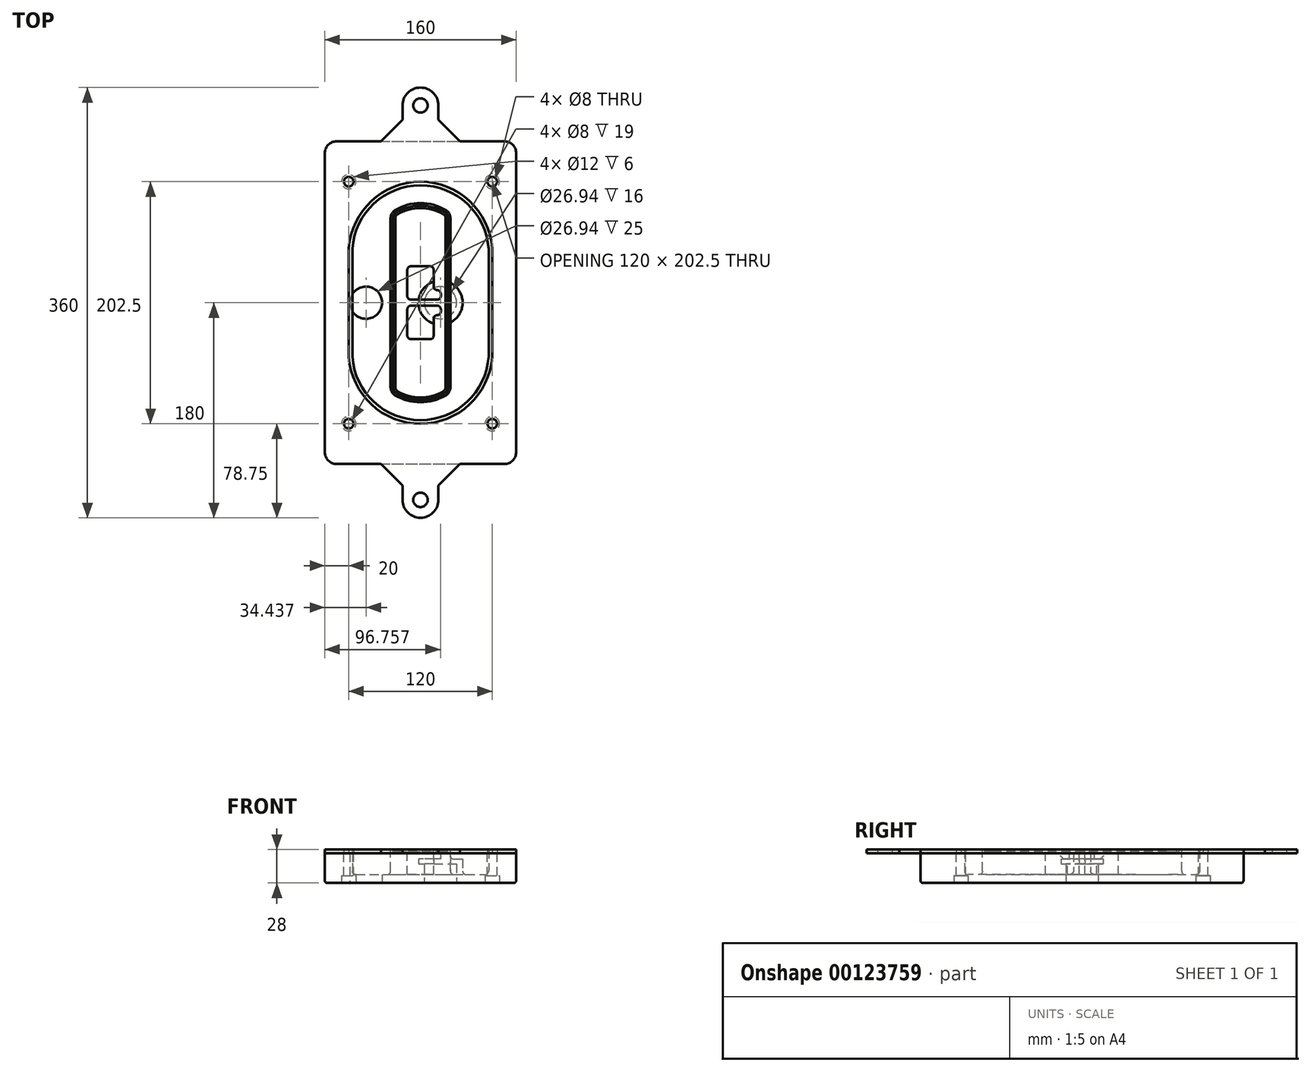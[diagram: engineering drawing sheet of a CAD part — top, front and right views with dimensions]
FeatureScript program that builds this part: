
annotation { "Feature Type Name" : "Feature", "Feature Type Description" : "" }
export const myFeature = defineFeature(function(context is Context, id is Id, definition is map)
    precondition{}
    {
        {
            var Q0;
            Q0=qCreatedBy(makeId("Top.planeOp"),FACE);
            var sketch = newSketch(context, id + "F0", { "sketchPlane" : qUnion([Q0])});
            skPoint(sketch, "E0.rect.middle", {"position": v(0, 0) * mm});
            skLineSegment(sketch, "E1.bottom", {"start": v(-70, -135) * mm, "end": v(70, -135) * mm});
            skLineSegment(sketch, "E1.top", {"start": v(-70, 135) * mm, "end": v(70, 135) * mm});
            skLineSegment(sketch, "E1.left", {"start": v(-80, -125) * mm, "end": v(-80, 125) * mm});
            skLineSegment(sketch, "E1.right", {"start": v(80, -125) * mm, "end": v(80, 125) * mm});
            skLineSegment(sketch, "E2", {"start": v(-80, 135) * mm, "end": v(80, -135) * mm, "construction": true});
            skLineSegment(sketch, "E3", {"start": v(80, 135) * mm, "end": v(-80, -135) * mm, "construction": true});
            skCircle(sketch, "E4", {"center": v(-60, 101.25) * mm, "radius": 4 * mm});
            skCircle(sketch, "E5", {"center": v(60, 101.25) * mm, "radius": 4 * mm});
            skCircle(sketch, "E6", {"center": v(60, -101.25) * mm, "radius": 4 * mm});
            skCircle(sketch, "E7", {"center": v(-60, -101.25) * mm, "radius": 4 * mm});
            skLineSegment(sketch, "E8", {"start": v(-60, 101.25) * mm, "end": v(60, 101.25) * mm, "construction": true});
            skLineSegment(sketch, "E9", {"start": v(60, 101.25) * mm, "end": v(60, -101.25) * mm, "construction": true});
            skLineSegment(sketch, "E10", {"start": v(60, -101.25) * mm, "end": v(-60, -101.25) * mm, "construction": true});
            skLineSegment(sketch, "E11", {"start": v(-60, -101.25) * mm, "end": v(-60, 101.25) * mm, "construction": true});
            skLineSegment(sketch, "E12", {"start": v(-60, 44.66) * mm, "end": v(-60, -44.66) * mm});
            skLineSegment(sketch, "E13", {"start": v(60, 44.66) * mm, "end": v(60, -44.66) * mm});
            skArc(sketch, "E14", {"start": v(59.98, 45.37) * mm, "mid": v(0, 101.25) * mm, "end": v(-59.98, 45.37) * mm});
            skArc(sketch, "E15", {"start": v(-59.98, -45.37) * mm, "mid": v(0, -101.25) * mm, "end": v(59.98, -45.37) * mm});
            skLineSegment(sketch, "E16", {"start": v(-60, 0) * mm, "end": v(60, 0) * mm, "construction": true});
            skPoint(sketch, "E17.visualSharp", {"position": v(-60, -45) * mm});
            skArc(sketch, "E17.filletArc", {"start": v(-60, -44.66) * mm, "mid": v(-60, -45.02) * mm, "end": v(-59.98, -45.37) * mm});
            skPoint(sketch, "E18.visualSharp", {"position": v(-60, 45) * mm});
            skArc(sketch, "E18.filletArc", {"start": v(-59.98, 45.37) * mm, "mid": v(-60, 45.02) * mm, "end": v(-60, 44.66) * mm});
            skPoint(sketch, "E19.visualSharp", {"position": v(60, 45) * mm});
            skArc(sketch, "E19.filletArc", {"start": v(60, 44.66) * mm, "mid": v(60, 45.02) * mm, "end": v(59.98, 45.37) * mm});
            skPoint(sketch, "E20.visualSharp", {"position": v(60, -45) * mm});
            skArc(sketch, "E20.filletArc", {"start": v(59.98, -45.37) * mm, "mid": v(60, -45.02) * mm, "end": v(60, -44.66) * mm});
            skPoint(sketch, "E21.visualSharp", {"position": v(-80, 135) * mm});
            skArc(sketch, "E21.filletArc", {"start": v(-70, 135) * mm, "mid": v(-77.07, 132.07) * mm, "end": v(-80, 125) * mm});
            skPoint(sketch, "E22.visualSharp", {"position": v(80, 135) * mm});
            skArc(sketch, "E22.filletArc", {"start": v(80, 125) * mm, "mid": v(77.07, 132.07) * mm, "end": v(70, 135) * mm});
            skPoint(sketch, "E23.visualSharp", {"position": v(80, -135) * mm});
            skArc(sketch, "E23.filletArc", {"start": v(70, -135) * mm, "mid": v(77.07, -132.07) * mm, "end": v(80, -125) * mm});
            skPoint(sketch, "E24.visualSharp", {"position": v(-80, -135) * mm});
            skArc(sketch, "E24.filletArc", {"start": v(-80, -125) * mm, "mid": v(-77.07, -132.07) * mm, "end": v(-70, -135) * mm});
            skArc(sketch, "E25.0", {"start": v(57, 44.66) * mm, "mid": v(57, 44.9) * mm, "end": v(56.98, 45.16) * mm});
            skLineSegment(sketch, "E25.1", {"start": v(57, 44.66) * mm, "end": v(57, -44.66) * mm});
            skArc(sketch, "E25.2", {"start": v(56.98, -45.16) * mm, "mid": v(57, -44.9) * mm, "end": v(57, -44.66) * mm});
            skArc(sketch, "E25.3", {"start": v(-56.98, -45.16) * mm, "mid": v(0, -98.25) * mm, "end": v(56.98, -45.16) * mm});
            skArc(sketch, "E25.4", {"start": v(-57, -44.66) * mm, "mid": v(-57, -44.9) * mm, "end": v(-56.98, -45.16) * mm});
            skArc(sketch, "E25.5", {"start": v(56.98, 45.16) * mm, "mid": v(0, 98.25) * mm, "end": v(-56.98, 45.16) * mm});
            skLineSegment(sketch, "E25.6", {"start": v(-57, 44.66) * mm, "end": v(-57, -44.66) * mm});
            skArc(sketch, "E25.7", {"start": v(-56.98, 45.16) * mm, "mid": v(-57, 44.9) * mm, "end": v(-57, 44.66) * mm});
            skArc(sketch, "E26.0", {"start": v(-63.97, 45.65) * mm, "mid": v(-64, 45.16) * mm, "end": v(-64, 44.66) * mm});
            skArc(sketch, "E26.1", {"start": v(63.97, 45.65) * mm, "mid": v(0, 105.25) * mm, "end": v(-63.97, 45.65) * mm});
            skArc(sketch, "E26.2", {"start": v(64, 44.66) * mm, "mid": v(64, 45.16) * mm, "end": v(63.97, 45.65) * mm});
            skLineSegment(sketch, "E26.3", {"start": v(64, 44.66) * mm, "end": v(64, -44.66) * mm});
            skArc(sketch, "E26.4", {"start": v(63.97, -45.65) * mm, "mid": v(64, -45.16) * mm, "end": v(64, -44.66) * mm});
            skLineSegment(sketch, "E26.5", {"start": v(-64, 44.66) * mm, "end": v(-64, -44.66) * mm});
            skArc(sketch, "E26.6", {"start": v(-63.97, -45.65) * mm, "mid": v(0, -105.25) * mm, "end": v(63.97, -45.65) * mm});
            skArc(sketch, "E26.7", {"start": v(-64, -44.66) * mm, "mid": v(-64, -45.16) * mm, "end": v(-63.97, -45.65) * mm});
            skSolve(sketch);
        }
        {
            var Q0;
            Q0=makeQuery(id+"F0.imprint","IMPRINT",FACE,{"disambiguationData":[TD([[makeQuery(id+"F0.imprint","IMPRINT",EDGE,{"derivedFrom":sQuery(id+"F0.wireOp",EDGE,"E1.bottom")}),1.0]])]});
            var Q1;
            Q1=makeQuery(id+"F0.imprint","IMPRINT",FACE,{"disambiguationData":[TD([[makeQuery(id+"F0.imprint","IMPRINT",EDGE,{"derivedFrom":sQuery(id+"F0.wireOp",EDGE,"E12")}),1.0]])]});
            var Q2;
            Q2=makeQuery(id+"F0.imprint","IMPRINT",FACE,{"disambiguationData":[TD([[makeQuery(id+"F0.imprint","IMPRINT",EDGE,{"derivedFrom":sQuery(id+"F0.wireOp",EDGE,"E25.0")}),1.0]])]});
            var Q3;
            Q3=makeQuery(id+"F0.imprint","IMPRINT",FACE,{"disambiguationData":[TD([[makeQuery(id+"F0.imprint","IMPRINT",EDGE,{"derivedFrom":sQuery(id+"F0.wireOp",EDGE,"E12")}),-1.0]])]});
            extrude(context, id + "F1", {"entities" : qUnion([Q0, Q1, Q2, Q3]), "oppositeDirection" : true, "depth" : 25 * mm});
        }
        {
            var Q0;
            Q0=makeQuery(id+"F0.imprint","IMPRINT",FACE,{"disambiguationData":[TD([[makeQuery(id+"F0.imprint","IMPRINT",EDGE,{"derivedFrom":sQuery(id+"F0.wireOp",EDGE,"E12")}),1.0]])]});
            extrude(context, id + "F2", {"entities" : qUnion([Q0]), "operationType" : NewBodyOperationType.ADD, "depth" : 3 * mm});
        }
        {
            var Q0;
            Q0=makeQuery(id+"F0.imprint","IMPRINT",FACE,{"disambiguationData":[TD([[makeQuery(id+"F0.imprint","IMPRINT",EDGE,{"derivedFrom":sQuery(id+"F0.wireOp",EDGE,"E25.0")}),1.0]])]});
            extrude(context, id + "F3", {"entities" : qUnion([Q0]), "operationType" : NewBodyOperationType.REMOVE, "oppositeDirection" : true, "depth" : 18 * mm});
        }
        {
            var Q0;
            Q0=makeQuery(id+"F2.opExtrude","CAP_FACE",FACE,{"disambiguationData":[OSD([sQuery(id+"F0.wireOp",EDGE,"E12"),sQuery(id+"F0.wireOp",EDGE,"E13"),sQuery(id+"F0.wireOp",EDGE,"E14"),sQuery(id+"F0.wireOp",EDGE,"E15"),sQuery(id+"F0.wireOp",EDGE,"E17.filletArc"),sQuery(id+"F0.wireOp",EDGE,"E18.filletArc"),sQuery(id+"F0.wireOp",EDGE,"E19.filletArc"),sQuery(id+"F0.wireOp",EDGE,"E20.filletArc"),sQuery(id+"F0.wireOp",EDGE,"E25.0"),sQuery(id+"F0.wireOp",EDGE,"E25.1"),sQuery(id+"F0.wireOp",EDGE,"E25.2"),sQuery(id+"F0.wireOp",EDGE,"E25.3"),sQuery(id+"F0.wireOp",EDGE,"E25.4"),sQuery(id+"F0.wireOp",EDGE,"E25.5"),sQuery(id+"F0.wireOp",EDGE,"E25.6"),sQuery(id+"F0.wireOp",EDGE,"E25.7")])],"isStart":false});
            var sketch = newSketch(context, id + "F4", { "sketchPlane" : qUnion([Q0])});
            skArc(sketch, "E27.0", {"start": v(-20.99, -77.65) * mm, "mid": v(0, -83.25) * mm, "end": v(20.99, -77.65) * mm});
            skArc(sketch, "E28.0", {"start": v(20.99, 77.65) * mm, "mid": v(0, 83.25) * mm, "end": v(-20.99, 77.65) * mm});
            skLineSegment(sketch, "E29", {"start": v(-25, 70.71) * mm, "end": v(-25, -70.71) * mm});
            skLineSegment(sketch, "E30", {"start": v(25, 70.71) * mm, "end": v(25, -70.71) * mm});
            skLineSegment(sketch, "E31", {"start": v(-25, 75.03) * mm, "end": v(25, 75.03) * mm, "construction": true});
            skLineSegment(sketch, "E32", {"start": v(-25, -75.03) * mm, "end": v(25, -75.03) * mm, "construction": true});
            skPoint(sketch, "E33.visualSharp", {"position": v(-25, 75.03) * mm});
            skArc(sketch, "E33.filletArc", {"start": v(-20.99, 77.65) * mm, "mid": v(-23.92, 74.72) * mm, "end": v(-25, 70.71) * mm});
            skPoint(sketch, "E34.visualSharp", {"position": v(25, 75.03) * mm});
            skArc(sketch, "E34.filletArc", {"start": v(25, 70.71) * mm, "mid": v(23.92, 74.72) * mm, "end": v(20.99, 77.65) * mm});
            skPoint(sketch, "E35.visualSharp", {"position": v(25, -75.03) * mm});
            skArc(sketch, "E35.filletArc", {"start": v(20.99, -77.65) * mm, "mid": v(23.92, -74.72) * mm, "end": v(25, -70.71) * mm});
            skPoint(sketch, "E36.visualSharp", {"position": v(-25, -75.03) * mm});
            skArc(sketch, "E36.filletArc", {"start": v(-25, -70.71) * mm, "mid": v(-23.92, -74.72) * mm, "end": v(-20.99, -77.65) * mm});
            skArc(sketch, "E37.0", {"start": v(56.98, 45.16) * mm, "mid": v(0, 98.25) * mm, "end": v(-56.98, 45.16) * mm});
            skArc(sketch, "E37.1", {"start": v(-56.98, 45.16) * mm, "mid": v(-57, 44.9) * mm, "end": v(-57, 44.66) * mm});
            skLineSegment(sketch, "E37.2", {"start": v(-57, 44.66) * mm, "end": v(-57, -44.66) * mm});
            skArc(sketch, "E37.3", {"start": v(-57, -44.66) * mm, "mid": v(-57, -44.9) * mm, "end": v(-56.98, -45.16) * mm});
            skArc(sketch, "E37.4", {"start": v(-56.98, -45.16) * mm, "mid": v(0, -98.25) * mm, "end": v(56.98, -45.16) * mm});
            skArc(sketch, "E37.5", {"start": v(56.98, -45.16) * mm, "mid": v(57, -44.9) * mm, "end": v(57, -44.66) * mm});
            skLineSegment(sketch, "E37.6", {"start": v(57, 44.66) * mm, "end": v(57, -44.66) * mm});
            skArc(sketch, "E37.7", {"start": v(57, 44.66) * mm, "mid": v(57, 44.9) * mm, "end": v(56.98, 45.16) * mm});
            skLineSegment(sketch, "E38.0", {"start": v(23, 70.71) * mm, "end": v(23, -70.71) * mm});
            skArc(sketch, "E38.1", {"start": v(19.99, -75.92) * mm, "mid": v(22.2, -73.72) * mm, "end": v(23, -70.71) * mm});
            skArc(sketch, "E38.2", {"start": v(-19.99, -75.92) * mm, "mid": v(0, -81.25) * mm, "end": v(19.99, -75.92) * mm});
            skArc(sketch, "E38.3", {"start": v(-23, -70.71) * mm, "mid": v(-22.2, -73.72) * mm, "end": v(-19.99, -75.92) * mm});
            skLineSegment(sketch, "E38.4", {"start": v(-23, 70.71) * mm, "end": v(-23, -70.71) * mm});
            skArc(sketch, "E38.5", {"start": v(23, 70.71) * mm, "mid": v(22.2, 73.72) * mm, "end": v(19.99, 75.92) * mm});
            skArc(sketch, "E38.6", {"start": v(-19.99, 75.92) * mm, "mid": v(-22.2, 73.72) * mm, "end": v(-23, 70.71) * mm});
            skArc(sketch, "E38.7", {"start": v(19.99, 75.92) * mm, "mid": v(0, 81.25) * mm, "end": v(-19.99, 75.92) * mm});
            skArc(sketch, "E39.0", {"start": v(21, 70.71) * mm, "mid": v(20.46, 72.72) * mm, "end": v(19, 74.18) * mm});
            skLineSegment(sketch, "E39.1", {"start": v(21, 70.71) * mm, "end": v(21, -70.71) * mm});
            skArc(sketch, "E39.2", {"start": v(19, -74.18) * mm, "mid": v(20.46, -72.72) * mm, "end": v(21, -70.71) * mm});
            skArc(sketch, "E39.3", {"start": v(-19, -74.18) * mm, "mid": v(0, -79.25) * mm, "end": v(19, -74.18) * mm});
            skArc(sketch, "E39.4", {"start": v(-21, -70.71) * mm, "mid": v(-20.46, -72.72) * mm, "end": v(-19, -74.18) * mm});
            skArc(sketch, "E39.5", {"start": v(19, 74.18) * mm, "mid": v(0, 79.25) * mm, "end": v(-19, 74.18) * mm});
            skLineSegment(sketch, "E39.6", {"start": v(-21, 70.71) * mm, "end": v(-21, -70.71) * mm});
            skArc(sketch, "E39.7", {"start": v(-19, 74.18) * mm, "mid": v(-20.46, 72.72) * mm, "end": v(-21, 70.71) * mm});
            skLineSegment(sketch, "E40", {"start": v(-25, 0) * mm, "end": v(25, 0) * mm, "construction": true});
            skLineSegment(sketch, "E41", {"start": v(-11, 5.5) * mm, "end": v(-11, 27.5) * mm});
            skLineSegment(sketch, "E42", {"start": v(-8, 30.5) * mm, "end": v(8, 30.5) * mm});
            skLineSegment(sketch, "E43", {"start": v(11, 27.5) * mm, "end": v(11, 13.5) * mm});
            skLineSegment(sketch, "E44", {"start": v(14, 10.5) * mm, "end": v(14, 10.5) * mm});
            skLineSegment(sketch, "E45", {"start": v(17, 7.5) * mm, "end": v(17, 5.5) * mm});
            skLineSegment(sketch, "E46", {"start": v(14, 2.5) * mm, "end": v(-8, 2.5) * mm});
            skPoint(sketch, "E47.visualSharp", {"position": v(-11, 30.5) * mm});
            skArc(sketch, "E47.filletArc", {"start": v(-8, 30.5) * mm, "mid": v(-10.12, 29.62) * mm, "end": v(-11, 27.5) * mm});
            skPoint(sketch, "E48.visualSharp", {"position": v(11, 30.5) * mm});
            skArc(sketch, "E48.filletArc", {"start": v(11, 27.5) * mm, "mid": v(10.12, 29.62) * mm, "end": v(8, 30.5) * mm});
            skPoint(sketch, "E49.visualSharp", {"position": v(11, 10.5) * mm});
            skArc(sketch, "E49.filletArc", {"start": v(11, 13.5) * mm, "mid": v(11.88, 11.38) * mm, "end": v(14, 10.5) * mm});
            skPoint(sketch, "E50.visualSharp", {"position": v(17, 10.5) * mm});
            skArc(sketch, "E50.filletArc", {"start": v(17, 7.5) * mm, "mid": v(16.12, 9.62) * mm, "end": v(14, 10.5) * mm});
            skPoint(sketch, "E51.visualSharp", {"position": v(17, 2.5) * mm});
            skArc(sketch, "E51.filletArc", {"start": v(14, 2.5) * mm, "mid": v(16.12, 3.38) * mm, "end": v(17, 5.5) * mm});
            skPoint(sketch, "E52.visualSharp", {"position": v(-11, 2.5) * mm});
            skArc(sketch, "E52.filletArc", {"start": v(-11, 5.5) * mm, "mid": v(-10.12, 3.38) * mm, "end": v(-8, 2.5) * mm});
            skLineSegment(sketch, "E53.0.MirrorCS", {"start": v(14, -2.5) * mm, "end": v(-8, -2.5) * mm});
            skArc(sketch, "E54.0.MirrorCS", {"start": v(-11, -5.5) * mm, "mid": v(-10.12, -3.38) * mm, "end": v(-8, -2.5) * mm});
            skLineSegment(sketch, "E55.0.MirrorCS", {"start": v(-11, -5.5) * mm, "end": v(-11, -27.5) * mm});
            skArc(sketch, "E56.0.MirrorCS", {"start": v(-8, -30.5) * mm, "mid": v(-10.12, -29.62) * mm, "end": v(-11, -27.5) * mm});
            skLineSegment(sketch, "E57.0.MirrorCS", {"start": v(-8, -30.5) * mm, "end": v(8, -30.5) * mm});
            skArc(sketch, "E58.0.MirrorCS", {"start": v(11, -27.5) * mm, "mid": v(10.12, -29.62) * mm, "end": v(8, -30.5) * mm});
            skLineSegment(sketch, "E59.0.MirrorCS", {"start": v(11, -27.5) * mm, "end": v(11, -13.5) * mm});
            skArc(sketch, "E60.0.MirrorCS", {"start": v(11, -13.5) * mm, "mid": v(11.88, -11.38) * mm, "end": v(14, -10.5) * mm});
            skArc(sketch, "E61.0.MirrorCS", {"start": v(17, -7.5) * mm, "mid": v(16.12, -9.62) * mm, "end": v(14, -10.5) * mm});
            skLineSegment(sketch, "E62.0.MirrorCS", {"start": v(17, -7.5) * mm, "end": v(17, -5.5) * mm});
            skArc(sketch, "E63.0.MirrorCS", {"start": v(14, -2.5) * mm, "mid": v(16.12, -3.38) * mm, "end": v(17, -5.5) * mm});
            skSolve(sketch);
        }
        {
            var Q0;
            Q0=makeQuery(id+"F4.imprint","IMPRINT",FACE,{"disambiguationData":[TD([[makeQuery(id+"F4.imprint","IMPRINT",EDGE,{"derivedFrom":sQuery(id+"F4.wireOp",EDGE,"E27.0")}),1.0]])]});
            var Q1;
            Q1=makeQuery(id+"F4.imprint","IMPRINT",FACE,{"disambiguationData":[TD([[makeQuery(id+"F4.imprint","IMPRINT",EDGE,{"derivedFrom":sQuery(id+"F4.wireOp",EDGE,"E38.0")}),-1.0]])]});
            var Q2;
            Q2=makeQuery(id+"F4.imprint","IMPRINT",FACE,{"disambiguationData":[TD([[makeQuery(id+"F4.imprint","IMPRINT",EDGE,{"derivedFrom":sQuery(id+"F4.wireOp",EDGE,"E39.0")}),1.0]])]});
            extrude(context, id + "F5", {"entities" : qUnion([Q0, Q1, Q2]), "operationType" : NewBodyOperationType.ADD, "endBound" : BoundingType.UP_TO_NEXT, "oppositeDirection" : true, "depth" : 25 * mm});
        }
        {
            var Q0;
            Q0=makeQuery(id+"F4.imprint","IMPRINT",FACE,{"disambiguationData":[TD([[makeQuery(id+"F4.imprint","IMPRINT",EDGE,{"derivedFrom":sQuery(id+"F4.wireOp",EDGE,"E38.0")}),-1.0]])]});
            extrude(context, id + "F6", {"entities" : qUnion([Q0]), "operationType" : NewBodyOperationType.REMOVE, "oppositeDirection" : true, "depth" : 2 * mm});
        }
        {
            var Q0;
            Q0=makeQuery(id+"F1.opExtrude","CAP_FACE",FACE,{"disambiguationData":[OSD([sQuery(id+"F0.wireOp",EDGE,"E1.bottom"),sQuery(id+"F0.wireOp",EDGE,"E1.top"),sQuery(id+"F0.wireOp",EDGE,"E1.left"),sQuery(id+"F0.wireOp",EDGE,"E1.right"),sQuery(id+"F0.wireOp",EDGE,"E4"),sQuery(id+"F0.wireOp",EDGE,"E5"),sQuery(id+"F0.wireOp",EDGE,"E6"),sQuery(id+"F0.wireOp",EDGE,"E7"),sQuery(id+"F0.wireOp",EDGE,"E21.filletArc"),sQuery(id+"F0.wireOp",EDGE,"E22.filletArc"),sQuery(id+"F0.wireOp",EDGE,"E23.filletArc"),sQuery(id+"F0.wireOp",EDGE,"E24.filletArc")])],"isStart":false});
            var sketch = newSketch(context, id + "F7", { "sketchPlane" : qUnion([Q0])});
            skCircle(sketch, "E64", {"center": v(16.76, 0) * mm, "radius": 13.47 * mm});
            skCircle(sketch, "E65", {"center": v(-45.56, 0) * mm, "radius": 13.47 * mm});
            skLineSegment(sketch, "E66", {"start": v(80, 0) * mm, "end": v(-80, 0) * mm});
            skCircle(sketch, "E67", {"center": v(16.76, 0) * mm, "radius": 18.47 * mm});
            skCircle(sketch, "E68", {"center": v(60, -101.25) * mm, "radius": 6 * mm});
            skCircle(sketch, "E69", {"center": v(-60, -101.25) * mm, "radius": 6 * mm});
            skCircle(sketch, "E70", {"center": v(-60, 101.25) * mm, "radius": 6 * mm});
            skCircle(sketch, "E71", {"center": v(60, 101.25) * mm, "radius": 6 * mm});
            skSolve(sketch);
        }
        {
            var Q0;
            {var subQ1=sQuery(id+"F7.wireOp",EDGE,"E66");var subQ4=sQuery(id+"F7.wireOp",EDGE,"E64");var subQ6=makeQuery(id+"F7.imprint","INTERSECT",VERTEX,{"disambiguationData":[OD(0.0)],"derivedFrom":[subQ4,subQ1]});Q0=makeQuery(id+"F7.imprint","IMPRINT",FACE,{"disambiguationData":[TD([[makeQuery(id+"F7.imprint","IMPRINT",EDGE,{"disambiguationData":[TD([[subQ6,-1.0]])],"derivedFrom":subQ4}),-1.0]])]});}
            var Q1;
            {var subQ0=sQuery(id+"F7.wireOp",EDGE,"E66");var subQ1=sQuery(id+"F7.wireOp",EDGE,"E64");var subQ3=makeQuery(id+"F7.imprint","INTERSECT",VERTEX,{"disambiguationData":[OD(0.0)],"derivedFrom":[subQ1,subQ0]});Q1=makeQuery(id+"F7.imprint","IMPRINT",FACE,{"disambiguationData":[TD([[makeQuery(id+"F7.imprint","IMPRINT",EDGE,{"disambiguationData":[TD([[subQ3,-1.0]])],"derivedFrom":subQ1}),1.0]])]});}
            var Q2;
            {var subQ0=sQuery(id+"F7.wireOp",EDGE,"E66");var subQ1=sQuery(id+"F7.wireOp",EDGE,"E64");var subQ3=makeQuery(id+"F7.imprint","INTERSECT",VERTEX,{"disambiguationData":[OD(0.0)],"derivedFrom":[subQ1,subQ0]});Q2=makeQuery(id+"F7.imprint","IMPRINT",FACE,{"disambiguationData":[TD([[makeQuery(id+"F7.imprint","IMPRINT",EDGE,{"disambiguationData":[TD([[subQ3,1.0]])],"derivedFrom":subQ1}),1.0]])]});}
            var Q3;
            {var subQ1=sQuery(id+"F7.wireOp",EDGE,"E66");var subQ4=sQuery(id+"F7.wireOp",EDGE,"E64");var subQ6=makeQuery(id+"F7.imprint","INTERSECT",VERTEX,{"disambiguationData":[OD(0.0)],"derivedFrom":[subQ4,subQ1]});Q3=makeQuery(id+"F7.imprint","IMPRINT",FACE,{"disambiguationData":[TD([[makeQuery(id+"F7.imprint","IMPRINT",EDGE,{"disambiguationData":[TD([[subQ6,1.0]])],"derivedFrom":subQ4}),-1.0]])]});}
            extrude(context, id + "F8", {"entities" : qUnion([Q0, Q1, Q2, Q3]), "operationType" : NewBodyOperationType.ADD, "oppositeDirection" : true, "depth" : 20 * mm});
        }
        {
            var Q0;
            {var subQ0=sQuery(id+"F7.wireOp",EDGE,"E66");var subQ1=sQuery(id+"F7.wireOp",EDGE,"E64");var subQ3=makeQuery(id+"F7.imprint","INTERSECT",VERTEX,{"disambiguationData":[OD(0.0)],"derivedFrom":[subQ1,subQ0]});Q0=makeQuery(id+"F7.imprint","IMPRINT",FACE,{"disambiguationData":[TD([[makeQuery(id+"F7.imprint","IMPRINT",EDGE,{"disambiguationData":[TD([[subQ3,-1.0]])],"derivedFrom":subQ1}),1.0]])]});}
            var Q1;
            {var subQ0=sQuery(id+"F7.wireOp",EDGE,"E66");var subQ1=sQuery(id+"F7.wireOp",EDGE,"E64");var subQ3=makeQuery(id+"F7.imprint","INTERSECT",VERTEX,{"disambiguationData":[OD(0.0)],"derivedFrom":[subQ1,subQ0]});Q1=makeQuery(id+"F7.imprint","IMPRINT",FACE,{"disambiguationData":[TD([[makeQuery(id+"F7.imprint","IMPRINT",EDGE,{"disambiguationData":[TD([[subQ3,1.0]])],"derivedFrom":subQ1}),1.0]])]});}
            extrude(context, id + "F9", {"entities" : qUnion([Q0, Q1]), "operationType" : NewBodyOperationType.REMOVE, "oppositeDirection" : true, "depth" : 16 * mm});
        }
        {
            var Q0;
            {var subQ0=sQuery(id+"F7.wireOp",EDGE,"E66");var subQ1=sQuery(id+"F7.wireOp",EDGE,"E65");var subQ3=makeQuery(id+"F7.imprint","INTERSECT",VERTEX,{"disambiguationData":[OD(0.0)],"derivedFrom":[subQ1,subQ0]});Q0=makeQuery(id+"F7.imprint","IMPRINT",FACE,{"disambiguationData":[TD([[makeQuery(id+"F7.imprint","IMPRINT",EDGE,{"disambiguationData":[TD([[subQ3,-1.0]])],"derivedFrom":subQ1}),1.0]])]});}
            var Q1;
            {var subQ0=sQuery(id+"F7.wireOp",EDGE,"E66");var subQ1=sQuery(id+"F7.wireOp",EDGE,"E65");var subQ3=makeQuery(id+"F7.imprint","INTERSECT",VERTEX,{"disambiguationData":[OD(0.0)],"derivedFrom":[subQ1,subQ0]});Q1=makeQuery(id+"F7.imprint","IMPRINT",FACE,{"disambiguationData":[TD([[makeQuery(id+"F7.imprint","IMPRINT",EDGE,{"disambiguationData":[TD([[subQ3,1.0]])],"derivedFrom":subQ1}),1.0]])]});}
            extrude(context, id + "F10", {"entities" : qUnion([Q0, Q1]), "operationType" : NewBodyOperationType.REMOVE, "oppositeDirection" : true, "depth" : 25 * mm});
        }
        {
            var Q0;
            Q0=makeQuery(id+"F7.imprint","IMPRINT",FACE,{"disambiguationData":[TD([[makeQuery(id+"F7.imprint","IMPRINT",EDGE,{"derivedFrom":sQuery(id+"F7.wireOp",EDGE,"E68")}),1.0]])]});
            var Q1;
            Q1=makeQuery(id+"F7.imprint","IMPRINT",FACE,{"disambiguationData":[TD([[makeQuery(id+"F7.imprint","IMPRINT",EDGE,{"derivedFrom":makeQuery(id+"F1.opExtrude","CAP_EDGE",EDGE,{"disambiguationData":[OSD([sQuery(id+"F0.wireOp",EDGE,"E5")])],"isStart":false})}),-1.0]])]});
            var Q2;
            Q2=makeQuery(id+"F7.imprint","IMPRINT",FACE,{"disambiguationData":[TD([[makeQuery(id+"F7.imprint","IMPRINT",EDGE,{"derivedFrom":sQuery(id+"F7.wireOp",EDGE,"E69")}),1.0]])]});
            var Q3;
            Q3=makeQuery(id+"F7.imprint","IMPRINT",FACE,{"disambiguationData":[TD([[makeQuery(id+"F7.imprint","IMPRINT",EDGE,{"derivedFrom":makeQuery(id+"F1.opExtrude","CAP_EDGE",EDGE,{"disambiguationData":[OSD([sQuery(id+"F0.wireOp",EDGE,"E4")])],"isStart":false})}),-1.0]])]});
            var Q4;
            Q4=makeQuery(id+"F7.imprint","IMPRINT",FACE,{"disambiguationData":[TD([[makeQuery(id+"F7.imprint","IMPRINT",EDGE,{"derivedFrom":sQuery(id+"F7.wireOp",EDGE,"E70")}),1.0]])]});
            var Q5;
            Q5=makeQuery(id+"F7.imprint","IMPRINT",FACE,{"disambiguationData":[TD([[makeQuery(id+"F7.imprint","IMPRINT",EDGE,{"derivedFrom":makeQuery(id+"F1.opExtrude","CAP_EDGE",EDGE,{"disambiguationData":[OSD([sQuery(id+"F0.wireOp",EDGE,"E7")])],"isStart":false})}),-1.0]])]});
            var Q6;
            Q6=makeQuery(id+"F7.imprint","IMPRINT",FACE,{"disambiguationData":[TD([[makeQuery(id+"F7.imprint","IMPRINT",EDGE,{"derivedFrom":sQuery(id+"F7.wireOp",EDGE,"E71")}),1.0]])]});
            var Q7;
            Q7=makeQuery(id+"F7.imprint","IMPRINT",FACE,{"disambiguationData":[TD([[makeQuery(id+"F7.imprint","IMPRINT",EDGE,{"derivedFrom":makeQuery(id+"F1.opExtrude","CAP_EDGE",EDGE,{"disambiguationData":[OSD([sQuery(id+"F0.wireOp",EDGE,"E6")])],"isStart":false})}),-1.0]])]});
            extrude(context, id + "F11", {"entities" : qUnion([Q0, Q1, Q2, Q3, Q4, Q5, Q6, Q7]), "operationType" : NewBodyOperationType.REMOVE, "oppositeDirection" : true, "depth" : 6 * mm});
        }
        {
            var Q0;
            Q0=makeQuery(id+"F9.boolean.opBoolean","COPY",FACE,{"derivedFrom":makeQuery(id+"F9.opExtrude","CAP_FACE",FACE,{"disambiguationData":[OSD([sQuery(id+"F7.wireOp",EDGE,"E64")])],"isStart":false})});
            var sketch = newSketch(context, id + "F12", { "sketchPlane" : qUnion([Q0])});
            skArc(sketch, "E72.0", {"start": v(11, 17.55) * mm, "mid": v(2.57, 11.82) * mm, "end": v(-1.54, 2.5) * mm});
            skArc(sketch, "E72.1", {"start": v(-1.54, -2.5) * mm, "mid": v(2.57, -11.82) * mm, "end": v(11, -17.55) * mm});
            skLineSegment(sketch, "E73", {"start": v(-1.54, -2.5) * mm, "end": v(14, -2.5) * mm});
            skLineSegment(sketch, "E74.0", {"start": v(14, 2.5) * mm, "end": v(-1.54, 2.5) * mm});
            skArc(sketch, "E74.1", {"start": v(14, 2.5) * mm, "mid": v(16.12, 3.38) * mm, "end": v(17, 5.5) * mm});
            skLineSegment(sketch, "E74.2", {"start": v(17, 7.5) * mm, "end": v(17, 5.5) * mm});
            skArc(sketch, "E74.3", {"start": v(17, 7.5) * mm, "mid": v(16.12, 9.62) * mm, "end": v(14, 10.5) * mm});
            skArc(sketch, "E74.4", {"start": v(11, 13.5) * mm, "mid": v(11.88, 11.38) * mm, "end": v(14, 10.5) * mm});
            skLineSegment(sketch, "E74.5", {"start": v(11, 17.55) * mm, "end": v(11, 13.5) * mm});
            skLineSegment(sketch, "E74.7", {"start": v(14, -2.5) * mm, "end": v(-1.54, -2.5) * mm});
            skArc(sketch, "E74.8", {"start": v(14, -2.5) * mm, "mid": v(16.12, -3.38) * mm, "end": v(17, -5.5) * mm});
            skLineSegment(sketch, "E74.9", {"start": v(17, -7.5) * mm, "end": v(17, -5.5) * mm});
            skArc(sketch, "E74.10", {"start": v(17, -7.5) * mm, "mid": v(16.12, -9.62) * mm, "end": v(14, -10.5) * mm});
            skArc(sketch, "E74.11", {"start": v(11, -13.5) * mm, "mid": v(11.88, -11.38) * mm, "end": v(14, -10.5) * mm});
            skLineSegment(sketch, "E74.12", {"start": v(11, -17.55) * mm, "end": v(11, -13.5) * mm});
            skPoint(sketch, "E75.orphan", {"position": v(11, -27.5) * mm});
            skPoint(sketch, "E76.orphan", {"position": v(-8, -2.5) * mm});
            skPoint(sketch, "E77.orphan", {"position": v(-8, 2.5) * mm});
            skPoint(sketch, "E78.orphan", {"position": v(11, 27.5) * mm});
            skSolve(sketch);
        }
        {
            var Q0;
            {var subQ7=sQuery(id+"F12.wireOp",EDGE,"E72.0");var subQ14=sQuery(id+"F12.wireOp",EDGE,"E72.1");var subQ16=sQuery(id+"F12.wireOp",EDGE,"E74.1");var subQ18=sQuery(id+"F12.wireOp",EDGE,"E74.8");Q0=qUnion([makeQuery(id+"F12.imprint","IMPRINT",FACE,{"disambiguationData":[TD([[makeQuery(id+"F12.imprint","IMPRINT",EDGE,{"derivedFrom":subQ7}),1.0]])]}),makeQuery(id+"F12.imprint","IMPRINT",FACE,{"disambiguationData":[TD([[makeQuery(id+"F12.imprint","IMPRINT",EDGE,{"derivedFrom":subQ14}),1.0]])]}),makeQuery(id+"F12.imprint","IMPRINT",FACE,{"disambiguationData":[TD([[makeQuery(id+"F12.imprint","IMPRINT",EDGE,{"derivedFrom":subQ16}),1.0]])]}),makeQuery(id+"F12.imprint","IMPRINT",FACE,{"disambiguationData":[TD([[makeQuery(id+"F12.imprint","IMPRINT",EDGE,{"derivedFrom":subQ18}),-1.0]])]})]);}
            var Q1;
            Q1=makeQuery(id+"F5.boolean.opBoolean","SPLIT",FACE,{"disambiguationData":[TD([makeQuery(id+"F5.opExtrude","SWEPT_FACE",FACE,{"disambiguationData":[OSD([sQuery(id+"F4.wireOp",EDGE,"E41")])]})])],"derivedFrom":makeQuery(id+"F3.boolean.opBoolean","COPY",FACE,{"derivedFrom":makeQuery(id+"F3.opExtrude","CAP_FACE",FACE,{"disambiguationData":[OSD([sQuery(id+"F0.wireOp",EDGE,"E25.0"),sQuery(id+"F0.wireOp",EDGE,"E25.1"),sQuery(id+"F0.wireOp",EDGE,"E25.2"),sQuery(id+"F0.wireOp",EDGE,"E25.3"),sQuery(id+"F0.wireOp",EDGE,"E25.4"),sQuery(id+"F0.wireOp",EDGE,"E25.5"),sQuery(id+"F0.wireOp",EDGE,"E25.6"),sQuery(id+"F0.wireOp",EDGE,"E25.7")])],"isStart":false})})});
            extrude(context, id + "F13", {"entities" : qUnion([Q0]), "operationType" : NewBodyOperationType.REMOVE, "endBound" : BoundingType.UP_TO_SURFACE, "endBoundEntityFace" : qUnion([Q1]), "depth" : 25 * mm});
        }
        {
            var Q0;
            Q0=makeQuery(id+"F3.boolean.opBoolean","COPY",EDGE,{"derivedFrom":makeQuery(id+"F3.opExtrude","CAP_EDGE",EDGE,{"disambiguationData":[OSD([sQuery(id+"F0.wireOp",EDGE,"E25.6")])],"isStart":false})});
            var Q1;
            Q1=makeQuery(id+"F8.boolean.opBoolean","INTERSECT",EDGE,{"derivedFrom":[makeQuery(id+"F5.opExtrude","SWEPT_FACE",FACE,{"disambiguationData":[OSD([sQuery(id+"F4.wireOp",EDGE,"E30")])]}),makeQuery(id+"F8.opExtrude","CAP_FACE",FACE,{"disambiguationData":[OSD([sQuery(id+"F7.wireOp",EDGE,"E67")])],"isStart":false})]});
            var Q2;
            Q2=makeQuery(id+"F8.boolean.opBoolean","INTERSECT",EDGE,{"disambiguationData":[OD(1.0)],"derivedFrom":[makeQuery(id+"F5.opExtrude","SWEPT_FACE",FACE,{"disambiguationData":[OSD([sQuery(id+"F4.wireOp",EDGE,"E30")])]}),makeQuery(id+"F8.opExtrude","SWEPT_FACE",FACE,{"disambiguationData":[OSD([sQuery(id+"F7.wireOp",EDGE,"E67")])]})]});
            var Q3;
            {var subQ0=sQuery(id+"F4.wireOp",EDGE,"E30");Q3=makeQuery(id+"F8.boolean.opBoolean","SPLIT",EDGE,{"disambiguationData":[TD([makeQuery(id+"F5.opExtrude","SWEPT_FACE",FACE,{"disambiguationData":[OSD([sQuery(id+"F4.wireOp",EDGE,"E35.filletArc")])]})])],"derivedFrom":makeQuery(id+"F5.opExtrude","CAP_EDGE",EDGE,{"disambiguationData":[OSD([subQ0])],"isStart":false})});}
            var Q4;
            {var subQ0=sQuery(id+"F0.wireOp",EDGE,"E25.7");var subQ1=sQuery(id+"F0.wireOp",EDGE,"E25.1");var subQ2=sQuery(id+"F0.wireOp",EDGE,"E25.6");var subQ3=sQuery(id+"F0.wireOp",EDGE,"E25.5");var subQ4=sQuery(id+"F0.wireOp",EDGE,"E25.4");var subQ5=sQuery(id+"F0.wireOp",EDGE,"E25.0");var subQ6=sQuery(id+"F0.wireOp",EDGE,"E25.2");var subQ7=sQuery(id+"F0.wireOp",EDGE,"E25.3");Q4=makeQuery(id+"F8.boolean.opBoolean","INTERSECT",EDGE,{"derivedFrom":[makeQuery(id+"F5.boolean.opBoolean","SPLIT",FACE,{"disambiguationData":[TD([makeQuery(id+"F2.opExtrude","SWEPT_FACE",FACE,{"disambiguationData":[OSD([subQ5])]})])],"derivedFrom":makeQuery(id+"F3.boolean.opBoolean","COPY",FACE,{"derivedFrom":makeQuery(id+"F3.opExtrude","CAP_FACE",FACE,{"disambiguationData":[OSD([subQ5,subQ1,subQ6,subQ7,subQ4,subQ3,subQ2,subQ0])],"isStart":false})})}),makeQuery(id+"F8.opExtrude","SWEPT_FACE",FACE,{"disambiguationData":[OSD([sQuery(id+"F7.wireOp",EDGE,"E67")])]})]});}
            var Q5;
            Q5=makeQuery(id+"F8.boolean.opBoolean","INTERSECT",EDGE,{"disambiguationData":[OD(0.0)],"derivedFrom":[makeQuery(id+"F5.opExtrude","SWEPT_FACE",FACE,{"disambiguationData":[OSD([sQuery(id+"F4.wireOp",EDGE,"E30")])]}),makeQuery(id+"F8.opExtrude","SWEPT_FACE",FACE,{"disambiguationData":[OSD([sQuery(id+"F7.wireOp",EDGE,"E67")])]})]});
            fillet(context, id + "F14", {"entities" : qUnion([Q0, Q1, Q2, Q3, Q4, Q5]), "radius" : 3 * mm, "tangentPropagation" : true, "allowEdgeOverflow" : false});
        }
        {
            var Q0;
            Q0=makeQuery(id+"F1.opExtrude","CAP_EDGE",EDGE,{"disambiguationData":[OSD([sQuery(id+"F0.wireOp",EDGE,"E1.bottom")])],"isStart":false});
            fillet(context, id + "F15", {"entities" : qUnion([Q0]), "radius" : 2 * mm, "tangentPropagation" : true, "allowEdgeOverflow" : false});
        }
        {
            var Q0;
            {var subQ0=sQuery(id+"F0.wireOp",EDGE,"E22.filletArc");var subQ1=sQuery(id+"F0.wireOp",EDGE,"E7");var subQ2=sQuery(id+"F0.wireOp",EDGE,"E6");var subQ3=sQuery(id+"F0.wireOp",EDGE,"E5");var subQ4=sQuery(id+"F0.wireOp",EDGE,"E4");var subQ5=sQuery(id+"F0.wireOp",EDGE,"E1.bottom");var subQ6=sQuery(id+"F0.wireOp",EDGE,"E21.filletArc");var subQ7=sQuery(id+"F0.wireOp",EDGE,"E1.top");var subQ8=sQuery(id+"F0.wireOp",EDGE,"E1.left");var subQ9=sQuery(id+"F0.wireOp",EDGE,"E1.right");var subQ10=sQuery(id+"F0.wireOp",EDGE,"E23.filletArc");var subQ11=sQuery(id+"F0.wireOp",EDGE,"E24.filletArc");Q0=makeQuery(id+"F2.boolean.opBoolean","SPLIT",FACE,{"disambiguationData":[TD([makeQuery(id+"F1.opExtrude","SWEPT_FACE",FACE,{"disambiguationData":[OSD([subQ5])]})])],"derivedFrom":makeQuery(id+"F1.opExtrude","CAP_FACE",FACE,{"disambiguationData":[OSD([subQ5,subQ7,subQ8,subQ9,subQ4,subQ3,subQ2,subQ1,subQ6,subQ0,subQ10,subQ11])],"isStart":true})});}
            var sketch = newSketch(context, id + "F16", { "sketchPlane" : qUnion([Q0])});
            skArc(sketch, "E79.0", {"start": v(-70, 135) * mm, "mid": v(-77.07, 132.07) * mm, "end": v(-80, 125) * mm});
            skLineSegment(sketch, "E79.1", {"start": v(-80, -125) * mm, "end": v(-80, 125) * mm});
            skArc(sketch, "E79.2", {"start": v(-80, -125) * mm, "mid": v(-77.07, -132.07) * mm, "end": v(-70, -135) * mm});
            skLineSegment(sketch, "E79.3", {"start": v(-70, -135) * mm, "end": v(70, -135) * mm});
            skArc(sketch, "E79.4", {"start": v(70, -135) * mm, "mid": v(77.07, -132.07) * mm, "end": v(80, -125) * mm});
            skLineSegment(sketch, "E79.5", {"start": v(80, -125) * mm, "end": v(80, 125) * mm});
            skArc(sketch, "E79.6", {"start": v(80, 125) * mm, "mid": v(77.07, 132.07) * mm, "end": v(70, 135) * mm});
            skLineSegment(sketch, "E79.7", {"start": v(-70, 135) * mm, "end": v(70, 135) * mm});
            skCircle(sketch, "E79.8", {"center": v(-60, 101.25) * mm, "radius": 4 * mm});
            skArc(sketch, "E79.9", {"start": v(-59.98, 45.37) * mm, "mid": v(-60, 45.02) * mm, "end": v(-60, 44.66) * mm});
            skArc(sketch, "E79.10", {"start": v(59.98, 45.37) * mm, "mid": v(0, 101.25) * mm, "end": v(-59.98, 45.37) * mm});
            skLineSegment(sketch, "E79.11", {"start": v(-60, 44.66) * mm, "end": v(-60, -44.66) * mm});
            skArc(sketch, "E79.12", {"start": v(-60, -44.66) * mm, "mid": v(-60, -45.02) * mm, "end": v(-59.98, -45.37) * mm});
            skArc(sketch, "E79.13", {"start": v(-59.98, -45.37) * mm, "mid": v(0, -101.25) * mm, "end": v(59.98, -45.37) * mm});
            skArc(sketch, "E79.14", {"start": v(59.98, -45.37) * mm, "mid": v(60, -45.02) * mm, "end": v(60, -44.66) * mm});
            skLineSegment(sketch, "E79.15", {"start": v(60, 44.66) * mm, "end": v(60, -44.66) * mm});
            skArc(sketch, "E79.16", {"start": v(60, 44.66) * mm, "mid": v(60, 45.02) * mm, "end": v(59.98, 45.37) * mm});
            skCircle(sketch, "E79.17", {"center": v(60, 101.25) * mm, "radius": 4 * mm});
            skCircle(sketch, "E79.18", {"center": v(60, -101.25) * mm, "radius": 4 * mm});
            skCircle(sketch, "E79.19", {"center": v(-60, -101.25) * mm, "radius": 4 * mm});
            skLineSegment(sketch, "E80", {"start": v(0, 135) * mm, "end": v(0, 165) * mm, "construction": true});
            skCircle(sketch, "E81", {"center": v(0, 165) * mm, "radius": 6 * mm});
            skArc(sketch, "E82", {"start": v(15, 165) * mm, "mid": v(0, 180) * mm, "end": v(-15, 165) * mm});
            skLineSegment(sketch, "E83", {"start": v(-15, 165) * mm, "end": v(-15, 153) * mm});
            skLineSegment(sketch, "E84", {"start": v(-15, 153) * mm, "end": v(-33, 135) * mm});
            skLineSegment(sketch, "E85", {"start": v(15, 165) * mm, "end": v(15, 153) * mm});
            skLineSegment(sketch, "E86", {"start": v(15, 153) * mm, "end": v(33, 135) * mm});
            skLineSegment(sketch, "E87", {"start": v(-80, 0) * mm, "end": v(80, 0) * mm, "construction": true});
            skLineSegment(sketch, "E88.MirrorCS", {"start": v(15, -153) * mm, "end": v(33, -135) * mm});
            skLineSegment(sketch, "E89.MirrorCS", {"start": v(-15, -153) * mm, "end": v(-33, -135) * mm});
            skLineSegment(sketch, "E90.MirrorCS", {"start": v(0, -135) * mm, "end": v(0, -165) * mm, "construction": true});
            skCircle(sketch, "E91.MirrorC", {"center": v(0, -165) * mm, "radius": 6 * mm});
            skLineSegment(sketch, "E92.MirrorCS", {"start": v(-15, -165) * mm, "end": v(-15, -153) * mm});
            skLineSegment(sketch, "E93.MirrorCS", {"start": v(15, -165) * mm, "end": v(15, -153) * mm});
            skArc(sketch, "E94.MirrorCS", {"start": v(15, -165) * mm, "mid": v(0, -180) * mm, "end": v(-15, -165) * mm});
            skSolve(sketch);
        }
        {
            var Q0;
            Q0 = qSketchRegion(id + "F16", true);
            var Q1;
            Q1=makeQuery(id+"F2.opExtrude","CAP_FACE",FACE,{"disambiguationData":[OSD([sQuery(id+"F0.wireOp",EDGE,"E12"),sQuery(id+"F0.wireOp",EDGE,"E13"),sQuery(id+"F0.wireOp",EDGE,"E14"),sQuery(id+"F0.wireOp",EDGE,"E15"),sQuery(id+"F0.wireOp",EDGE,"E17.filletArc"),sQuery(id+"F0.wireOp",EDGE,"E18.filletArc"),sQuery(id+"F0.wireOp",EDGE,"E19.filletArc"),sQuery(id+"F0.wireOp",EDGE,"E20.filletArc"),sQuery(id+"F0.wireOp",EDGE,"E25.0"),sQuery(id+"F0.wireOp",EDGE,"E25.1"),sQuery(id+"F0.wireOp",EDGE,"E25.2"),sQuery(id+"F0.wireOp",EDGE,"E25.3"),sQuery(id+"F0.wireOp",EDGE,"E25.4"),sQuery(id+"F0.wireOp",EDGE,"E25.5"),sQuery(id+"F0.wireOp",EDGE,"E25.6"),sQuery(id+"F0.wireOp",EDGE,"E25.7")])],"isStart":false});
            extrude(context, id + "F17", {"entities" : qUnion([Q0]), "endBound" : BoundingType.UP_TO_SURFACE, "endBoundEntityFace" : qUnion([Q1]), "depth" : 25 * mm});
        }
    });
